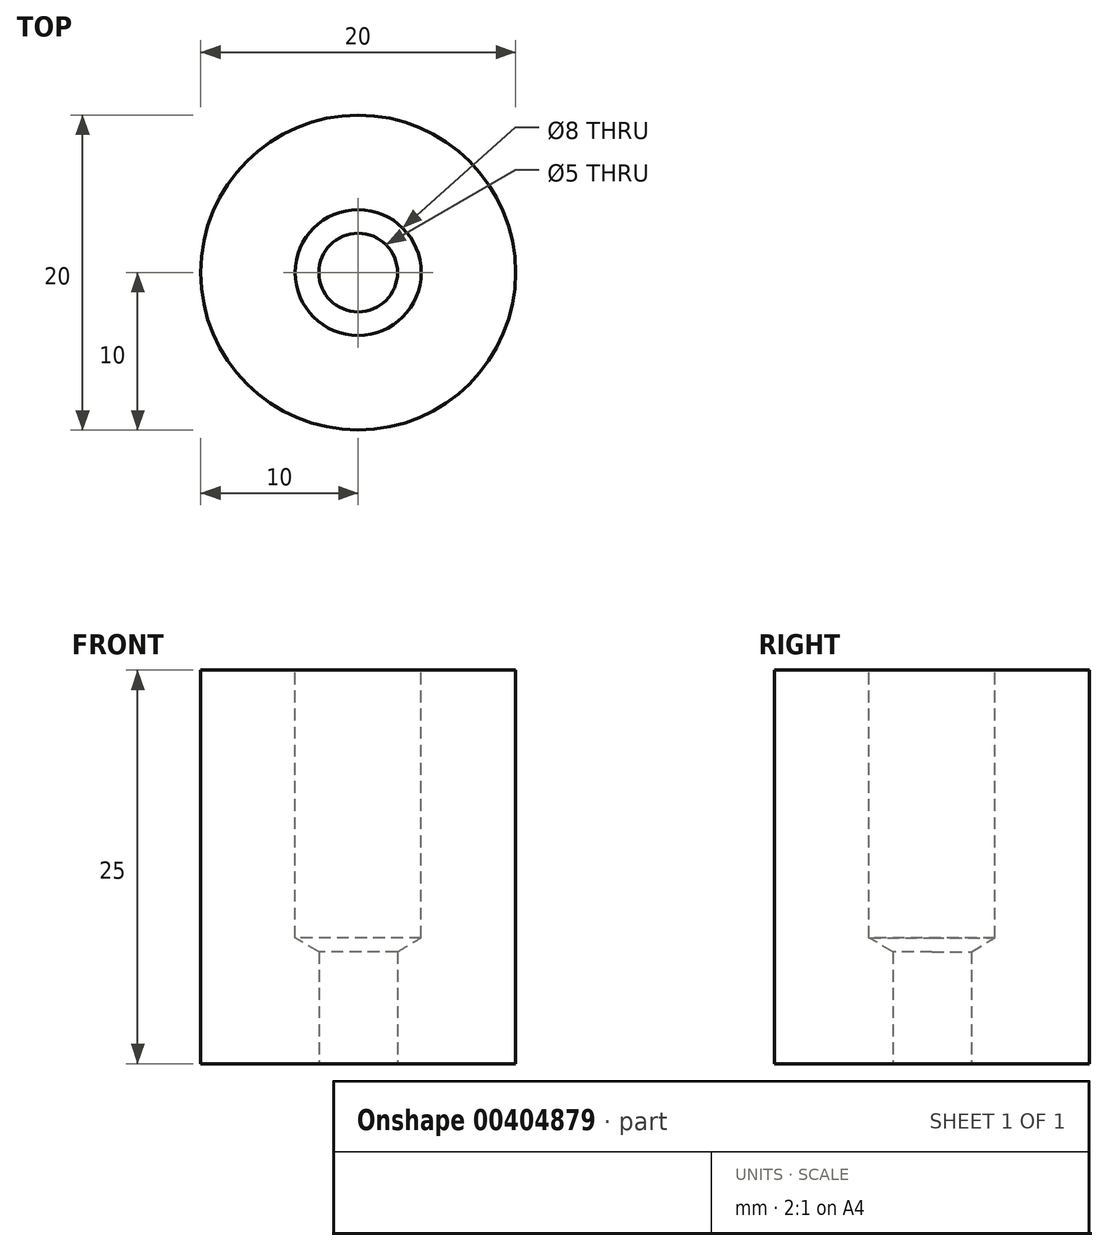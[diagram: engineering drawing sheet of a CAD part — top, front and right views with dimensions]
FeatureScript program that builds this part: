
annotation { "Feature Type Name" : "Feature", "Feature Type Description" : "" }
export const myFeature = defineFeature(function(context is Context, id is Id, definition is map)
    precondition{}
    {
        {
            var Q0;
            Q0=qCreatedBy(makeId("Front.planeOp"),FACE);
            var sketch = newSketch(context, id + "F0", { "sketchPlane" : qUnion([Q0])});
            skLineSegment(sketch, "E0.bottom", {"start": v(-10, 25) * mm, "end": v(0, 25) * mm});
            skLineSegment(sketch, "E0.top", {"start": v(-10, 0) * mm, "end": v(0, 0) * mm});
            skLineSegment(sketch, "E0.left", {"start": v(-10, 25) * mm, "end": v(-10, 0) * mm});
            skLineSegment(sketch, "E0.right", {"start": v(0, 25) * mm, "end": v(0, 0) * mm});
            skSolve(sketch);
        }
        {
            var Q0;
            Q0=qSketchRegion(id+"F0",true);
            var Q1;
            Q1=sQuery(id+"F0.wireOp",EDGE,"E0.right");
            revolve(context, id + "F1", {"entities" : qUnion([Q0]), "axis" : qUnion([Q1]), "revolveType" : RevolveType.FULL});
        }
        {
            var Q0;
            Q0=makeQuery(id+"F1.opRevolve","SWEPT_FACE",FACE,{"disambiguationData":[OSD([sQuery(id+"F0.wireOp",EDGE,"E0.bottom")])]});
            var sketch = newSketch(context, id + "F2", { "sketchPlane" : qUnion([Q0])});
            skPoint(sketch, "E1", {"position": v(0, 0) * mm});
            skSolve(sketch);
        }
        {
            var Q0;
            Q0=sQuery(id+"F2.wireOp",VERTEX,"E1");
            var Q1;
            Q1=makeQuery(id+"F1.opRevolve","SWEPT_BODY",BODY,{"disambiguationData":[OSD([sQuery(id+"F0.wireOp",EDGE,"E0.bottom"),sQuery(id+"F0.wireOp",EDGE,"E0.top"),sQuery(id+"F0.wireOp",EDGE,"E0.left"),sQuery(id+"F0.wireOp",EDGE,"E0.right")])]});
            hole(context, id + "F3", {"style" : HoleStyle.SIMPLE, "endStyle" : HoleEndStyle.BLIND, "holeDiameter" : 8 * mm, "holeDepth" : 17 * mm, "tappedDepth" : 12 * mm, "tapClearance" : 3, "locations" : qUnion([Q0]), "scope" : qUnion([Q1])});
        }
        {
            var Q0;
            Q0=makeQuery(id+"F1.opRevolve","SWEPT_FACE",FACE,{"disambiguationData":[OSD([sQuery(id+"F0.wireOp",EDGE,"E0.top")])]});
            var sketch = newSketch(context, id + "F4", { "sketchPlane" : qUnion([Q0])});
            skPoint(sketch, "E2", {"position": v(0, 0) * mm});
            skSolve(sketch);
        }
        {
            var Q0;
            Q0=sQuery(id+"F4.wireOp",VERTEX,"E2");
            var Q1;
            Q1=makeQuery(id+"F1.opRevolve","SWEPT_BODY",BODY,{"disambiguationData":[OSD([sQuery(id+"F0.wireOp",EDGE,"E0.bottom"),sQuery(id+"F0.wireOp",EDGE,"E0.top"),sQuery(id+"F0.wireOp",EDGE,"E0.left"),sQuery(id+"F0.wireOp",EDGE,"E0.right")])]});
            hole(context, id + "F5", {"style" : HoleStyle.SIMPLE, "endStyle" : HoleEndStyle.THROUGH, "holeDiameter" : 5 * mm, "tappedDepth" : 12 * mm, "tapClearance" : 3, "locations" : qUnion([Q0]), "scope" : qUnion([Q1])});
        }
    });
